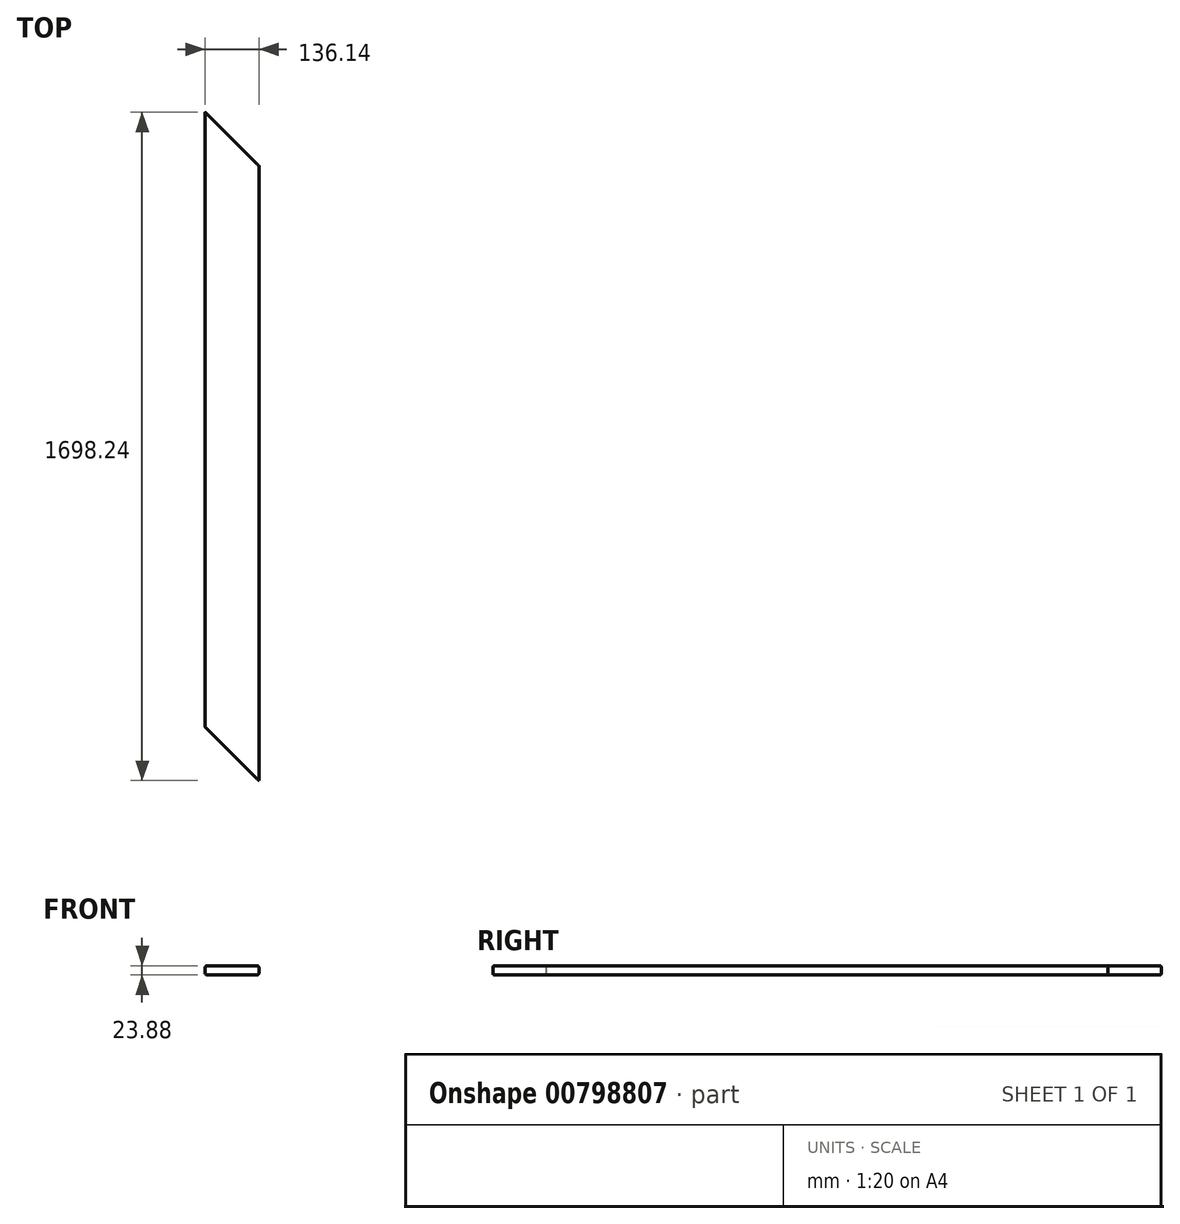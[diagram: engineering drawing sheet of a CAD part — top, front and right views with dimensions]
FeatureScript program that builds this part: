
annotation { "Feature Type Name" : "Feature", "Feature Type Description" : "" }
export const myFeature = defineFeature(function(context is Context, id is Id, definition is map)
    precondition{}
    {
        {
            var Q0;
            Q0=qCreatedBy(makeId("Front.planeOp"),FACE);
            var sketch = newSketch(context, id + "F0", { "sketchPlane" : qUnion([Q0])});
            skLineSegment(sketch, "E0.bottom", {"start": v(-63.25, 11.94) * mm, "end": v(63.25, 11.94) * mm});
            skLineSegment(sketch, "E0.top", {"start": v(-63.25, -11.94) * mm, "end": v(63.25, -11.94) * mm});
            skLineSegment(sketch, "E0.left", {"start": v(-68.07, 7.11) * mm, "end": v(-68.07, -7.11) * mm});
            skLineSegment(sketch, "E0.right", {"start": v(68.07, 7.11) * mm, "end": v(68.07, -7.11) * mm});
            skPoint(sketch, "E0.middle", {"position": v(0, 0) * mm});
            skPoint(sketch, "E1.visualSharp", {"position": v(-68.07, 11.94) * mm});
            skArc(sketch, "E1.filletArc", {"start": v(-63.25, 11.94) * mm, "mid": v(-66.66, 10.52) * mm, "end": v(-68.07, 7.11) * mm});
            skPoint(sketch, "E2.visualSharp", {"position": v(68.07, 11.94) * mm});
            skArc(sketch, "E2.filletArc", {"start": v(68.07, 7.11) * mm, "mid": v(66.66, 10.52) * mm, "end": v(63.25, 11.94) * mm});
            skPoint(sketch, "E3.visualSharp", {"position": v(68.07, -11.94) * mm});
            skArc(sketch, "E3.filletArc", {"start": v(63.25, -11.94) * mm, "mid": v(66.66, -10.52) * mm, "end": v(68.07, -7.11) * mm});
            skPoint(sketch, "E4.visualSharp", {"position": v(-68.07, -11.94) * mm});
            skArc(sketch, "E4.filletArc", {"start": v(-68.07, -7.11) * mm, "mid": v(-66.66, -10.52) * mm, "end": v(-63.25, -11.94) * mm});
            skSolve(sketch);
        }
        {
            var Q0;
            Q0=makeQuery(id+"F0.imprint","IMPRINT",FACE,{"disambiguationData":[TD([[makeQuery(id+"F0.imprint","IMPRINT",EDGE,{"derivedFrom":sQuery(id+"F0.wireOp",EDGE,"E0.bottom")}),-1.0]])]});
            extrude(context, id + "F1", {"entities" : qUnion([Q0]), "endBound" : BoundingType.SYMMETRIC, "depth" : 1698.24 * mm, "offsetDistance" : 25.4 * mm});
        }
        {
            var Q0;
            Q0=makeQuery(id+"F1.opExtrude","SWEPT_FACE",FACE,{"disambiguationData":[OSD([sQuery(id+"F0.wireOp",EDGE,"E0.bottom")])]});
            var sketch = newSketch(context, id + "F2", { "sketchPlane" : qUnion([Q0])});
            skLineSegment(sketch, "E5", {"start": v(68.07, -849.12) * mm, "end": v(-68.07, -849.12) * mm});
            skLineSegment(sketch, "E6", {"start": v(-68.07, -849.12) * mm, "end": v(-68.07, -712.98) * mm});
            skLineSegment(sketch, "E7", {"start": v(-68.07, -712.98) * mm, "end": v(68.07, -849.12) * mm});
            skLineSegment(sketch, "E8", {"start": v(-68.07, 849.12) * mm, "end": v(68.07, 849.12) * mm});
            skLineSegment(sketch, "E9", {"start": v(68.07, 849.12) * mm, "end": v(68.07, 712.98) * mm});
            skLineSegment(sketch, "E10", {"start": v(68.07, 712.98) * mm, "end": v(-68.07, 849.12) * mm});
            skSolve(sketch);
        }
        {
            var Q0;
            Q0 = qSketchRegion(id + "F2", true);
            extrude(context, id + "F3", {"entities" : qUnion([Q0]), "operationType" : NewBodyOperationType.REMOVE, "endBound" : BoundingType.THROUGH_ALL, "oppositeDirection" : true, "depth" : 25.4 * mm, "offsetDistance" : 25.4 * mm});
        }
    });
